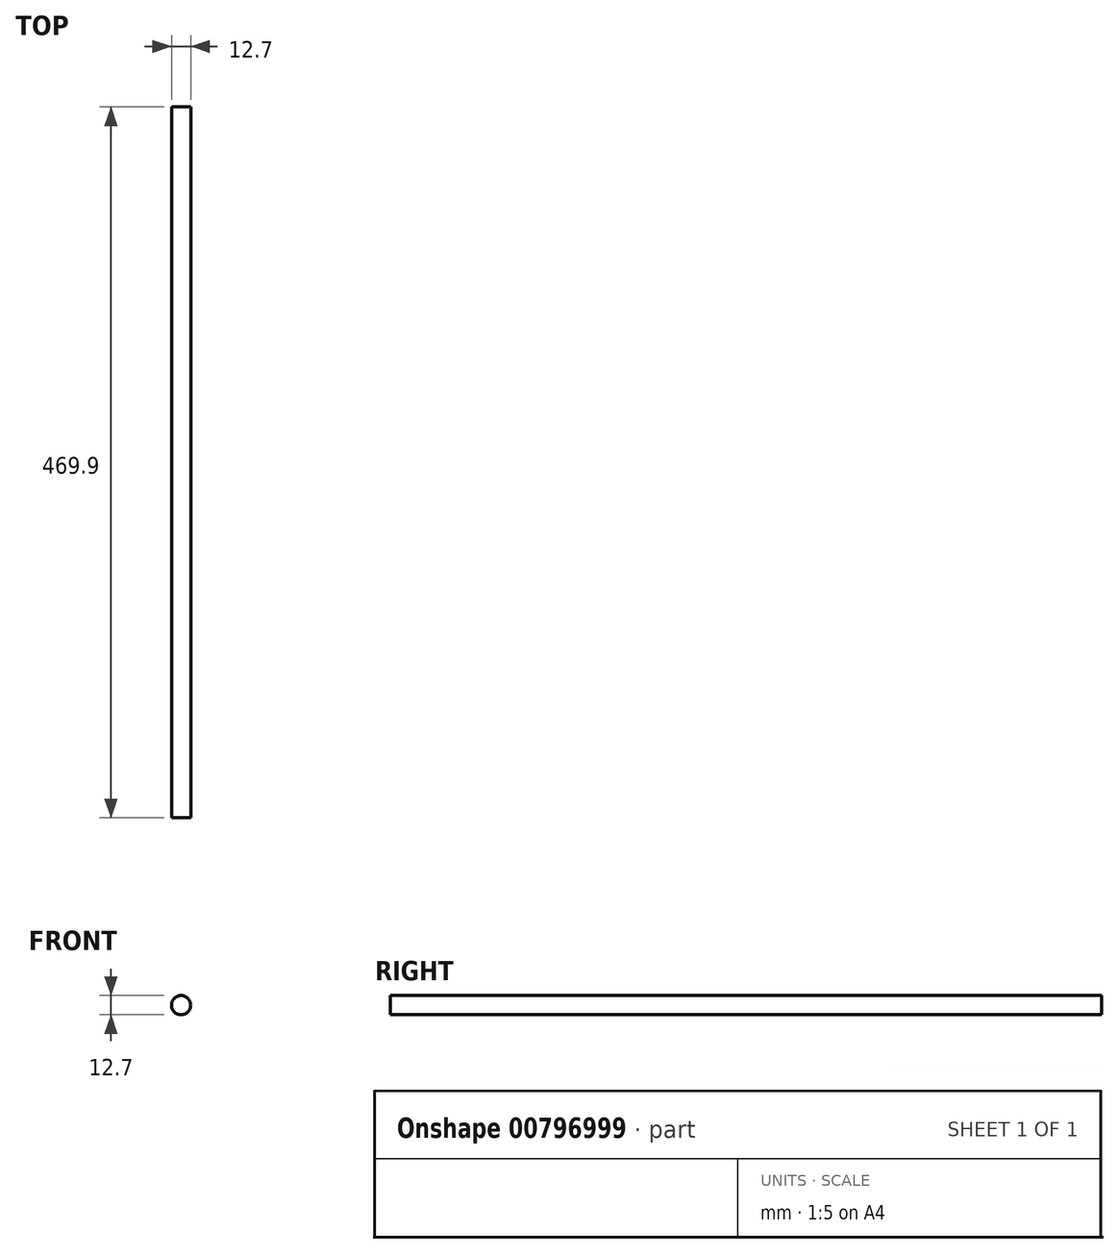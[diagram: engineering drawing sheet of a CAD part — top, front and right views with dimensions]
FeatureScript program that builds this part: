
annotation { "Feature Type Name" : "Feature", "Feature Type Description" : "" }
export const myFeature = defineFeature(function(context is Context, id is Id, definition is map)
    precondition{}
    {
        {
            var Q0;
            Q0=qCreatedBy(makeId("Front.planeOp"),FACE);
            var sketch = newSketch(context, id + "F0", { "sketchPlane" : qUnion([Q0])});
            skCircle(sketch, "E0", {"center": v(0, 0) * mm, "radius": 6.35 * mm});
            skSolve(sketch);
        }
        {
            var Q0;
            Q0=makeQuery(id+"F0.imprint","IMPRINT",FACE,{"disambiguationData":[TD([[makeQuery(id+"F0.imprint","IMPRINT",EDGE,{"derivedFrom":sQuery(id+"F0.wireOp",EDGE,"E0")}),1.0]])]});
            extrude(context, id + "F1", {"entities" : qUnion([Q0]), "flatOperationType" : FlatOperationType.REMOVE, "depth" : 469.9 * mm, "offsetDistance" : 25.4 * mm, "domain" : OperationDomain.MODEL});
        }
    });
